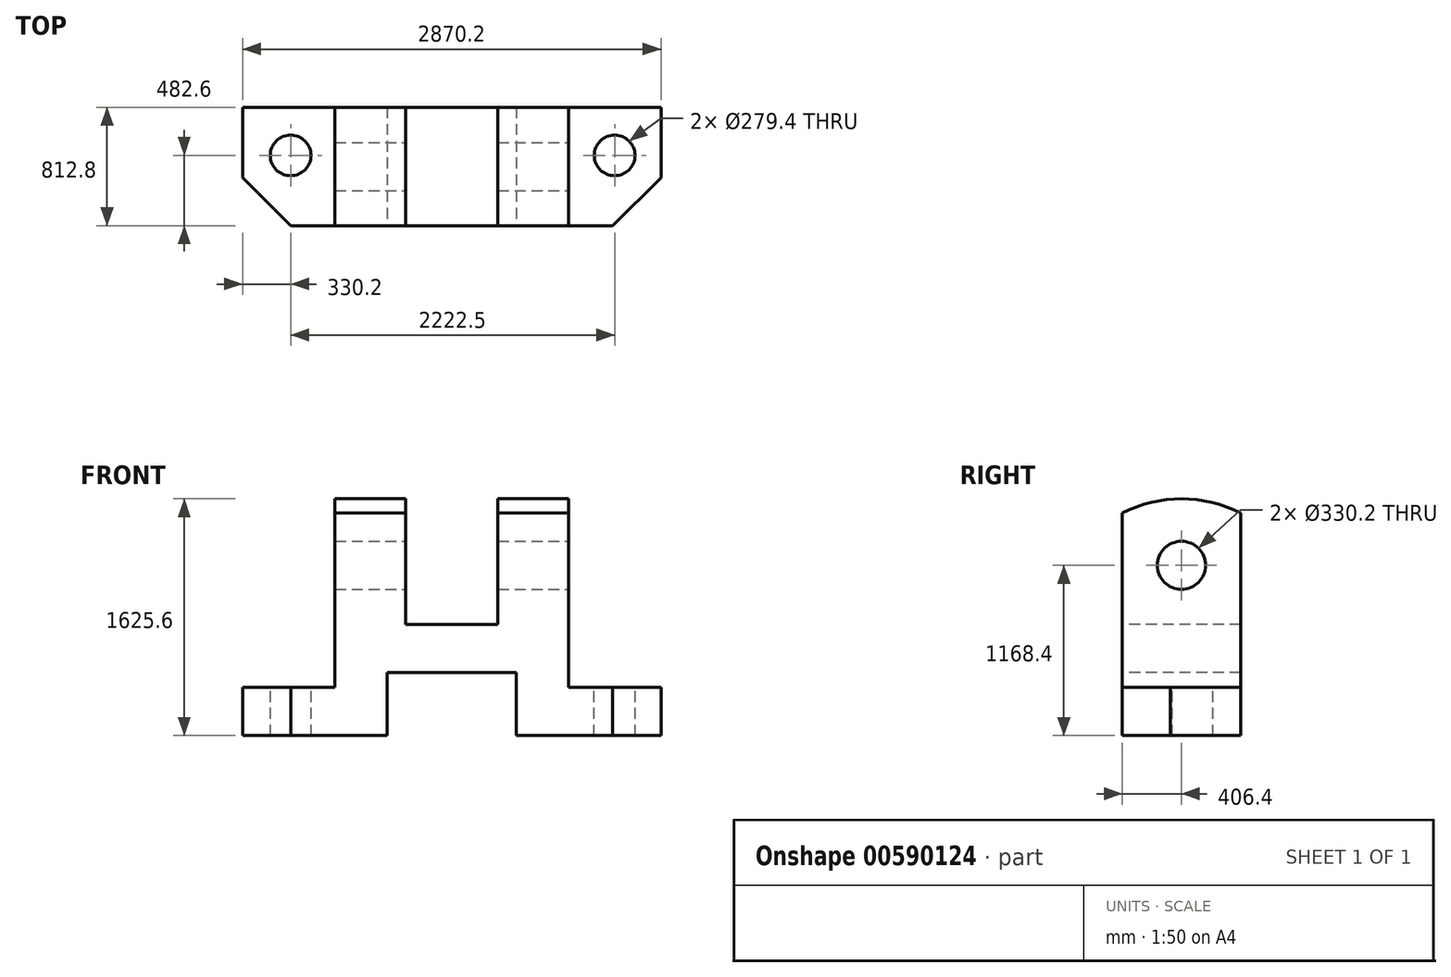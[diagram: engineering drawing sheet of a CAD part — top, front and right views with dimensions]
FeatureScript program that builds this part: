
annotation { "Feature Type Name" : "Feature", "Feature Type Description" : "" }
export const myFeature = defineFeature(function(context is Context, id is Id, definition is map)
    precondition{}
    {
        {
            var Q0;
            Q0=qCreatedBy(makeId("Front.planeOp"),FACE);
            var sketch = newSketch(context, id + "F0", { "sketchPlane" : qUnion([Q0])});
            skLineSegment(sketch, "E0.bottom", {"start": v(1435.1, 165.1) * mm, "end": v(-1435.1, 165.1) * mm});
            skLineSegment(sketch, "E0.top", {"start": v(1435.1, -165.1) * mm, "end": v(-1435.1, -165.1) * mm});
            skLineSegment(sketch, "E0.left", {"start": v(1435.1, 165.1) * mm, "end": v(1435.1, -165.1) * mm});
            skLineSegment(sketch, "E0.right", {"start": v(-1435.1, 165.1) * mm, "end": v(-1435.1, -165.1) * mm});
            skPoint(sketch, "E0.middle", {"position": v(0, 0) * mm});
            skSolve(sketch);
        }
        {
            var Q0;
            Q0=qSketchRegion(id+"F0",true);
            extrude(context, id + "F1", {"entities" : qUnion([Q0]), "depth" : 25.4 * mm});
        }
        {
            var Q0;
            Q0=qSketchRegion(id+"F0",true);
            extrude(context, id + "F2", {"entities" : qUnion([Q0]), "operationType" : NewBodyOperationType.ADD, "depth" : 812.8 * mm});
        }
        {
            var Q0;
            Q0=makeQuery(id+"F2.opExtrude","CAP_FACE",FACE,{"disambiguationData":[OSD([sQuery(id+"F0.wireOp",EDGE,"E0.bottom"),sQuery(id+"F0.wireOp",EDGE,"E0.top"),sQuery(id+"F0.wireOp",EDGE,"E0.left"),sQuery(id+"F0.wireOp",EDGE,"E0.right")])],"isStart":false});
            var sketch = newSketch(context, id + "F3", { "sketchPlane" : qUnion([Q0])});
            skLineSegment(sketch, "E1.bottom", {"start": v(-800.1, 165.1) * mm, "end": v(-317.5, 165.1) * mm});
            skLineSegment(sketch, "E1.top", {"start": v(-800.1, 1460.5) * mm, "end": v(-317.5, 1460.5) * mm});
            skLineSegment(sketch, "E1.left", {"start": v(-800.1, 165.1) * mm, "end": v(-800.1, 1460.5) * mm});
            skLineSegment(sketch, "E1.right", {"start": v(-317.5, 165.1) * mm, "end": v(-317.5, 1460.5) * mm});
            skLineSegment(sketch, "E2.bottom", {"start": v(317.5, 165.1) * mm, "end": v(800.1, 165.1) * mm});
            skLineSegment(sketch, "E2.top", {"start": v(317.5, 1460.5) * mm, "end": v(800.1, 1460.5) * mm});
            skLineSegment(sketch, "E2.left", {"start": v(317.5, 165.1) * mm, "end": v(317.5, 1460.5) * mm});
            skLineSegment(sketch, "E2.right", {"start": v(800.1, 165.1) * mm, "end": v(800.1, 1460.5) * mm});
            skSolve(sketch);
        }
        {
            var Q0;
            Q0=qSketchRegion(id+"F3",true);
            extrude(context, id + "F4", {"entities" : qUnion([Q0]), "operationType" : NewBodyOperationType.ADD, "oppositeDirection" : true, "depth" : 812.8 * mm});
        }
        {
            var Q0;
            Q0=makeQuery(id+"F4.boolean.opBoolean","MERGE",FACE,{"derivedFrom":[makeQuery(id+"F2.opExtrude","CAP_FACE",FACE,{"disambiguationData":[OSD([sQuery(id+"F0.wireOp",EDGE,"E0.bottom"),sQuery(id+"F0.wireOp",EDGE,"E0.top"),sQuery(id+"F0.wireOp",EDGE,"E0.left"),sQuery(id+"F0.wireOp",EDGE,"E0.right")])],"isStart":false}),makeQuery(id+"F4.opExtrude","CAP_FACE",FACE,{"disambiguationData":[OSD([sQuery(id+"F3.wireOp",EDGE,"E1.bottom"),sQuery(id+"F3.wireOp",EDGE,"E1.top"),sQuery(id+"F3.wireOp",EDGE,"E1.left"),sQuery(id+"F3.wireOp",EDGE,"E1.right")])],"isStart":true}),makeQuery(id+"F4.opExtrude","CAP_FACE",FACE,{"disambiguationData":[OSD([sQuery(id+"F3.wireOp",EDGE,"E2.bottom"),sQuery(id+"F3.wireOp",EDGE,"E2.top"),sQuery(id+"F3.wireOp",EDGE,"E2.left"),sQuery(id+"F3.wireOp",EDGE,"E2.right")])],"isStart":true})]});
            var sketch = newSketch(context, id + "F5", { "sketchPlane" : qUnion([Q0])});
            skLineSegment(sketch, "E3.bottom", {"start": v(-317.5, 165.1) * mm, "end": v(317.5, 165.1) * mm});
            skLineSegment(sketch, "E3.top", {"start": v(-317.5, 596.9) * mm, "end": v(317.5, 596.9) * mm});
            skLineSegment(sketch, "E3.left", {"start": v(-317.5, 165.1) * mm, "end": v(-317.5, 596.9) * mm});
            skLineSegment(sketch, "E3.right", {"start": v(317.5, 165.1) * mm, "end": v(317.5, 596.9) * mm});
            skSolve(sketch);
        }
        {
            var Q0;
            Q0=qSketchRegion(id+"F5",true);
            extrude(context, id + "F6", {"entities" : qUnion([Q0]), "operationType" : NewBodyOperationType.ADD, "oppositeDirection" : true, "depth" : 812.8 * mm});
        }
        {
            var Q0;
            Q0=makeQuery(id+"F6.boolean.opBoolean","MERGE",FACE,{"derivedFrom":[makeQuery(id+"F4.boolean.opBoolean","MERGE",FACE,{"derivedFrom":[makeQuery(id+"F2.opExtrude","CAP_FACE",FACE,{"disambiguationData":[OSD([sQuery(id+"F0.wireOp",EDGE,"E0.bottom"),sQuery(id+"F0.wireOp",EDGE,"E0.top"),sQuery(id+"F0.wireOp",EDGE,"E0.left"),sQuery(id+"F0.wireOp",EDGE,"E0.right")])],"isStart":false}),makeQuery(id+"F4.opExtrude","CAP_FACE",FACE,{"disambiguationData":[OSD([sQuery(id+"F3.wireOp",EDGE,"E1.bottom"),sQuery(id+"F3.wireOp",EDGE,"E1.top"),sQuery(id+"F3.wireOp",EDGE,"E1.left"),sQuery(id+"F3.wireOp",EDGE,"E1.right")])],"isStart":true}),makeQuery(id+"F4.opExtrude","CAP_FACE",FACE,{"disambiguationData":[OSD([sQuery(id+"F3.wireOp",EDGE,"E2.bottom"),sQuery(id+"F3.wireOp",EDGE,"E2.top"),sQuery(id+"F3.wireOp",EDGE,"E2.left"),sQuery(id+"F3.wireOp",EDGE,"E2.right")])],"isStart":true})]}),makeQuery(id+"F6.opExtrude","CAP_FACE",FACE,{"disambiguationData":[OSD([sQuery(id+"F5.wireOp",EDGE,"E3.bottom"),sQuery(id+"F5.wireOp",EDGE,"E3.top"),sQuery(id+"F5.wireOp",EDGE,"E3.left"),sQuery(id+"F5.wireOp",EDGE,"E3.right")])],"isStart":true})]});
            var sketch = newSketch(context, id + "F7", { "sketchPlane" : qUnion([Q0])});
            skLineSegment(sketch, "E4.bottom", {"start": v(-444.5, -165.1) * mm, "end": v(444.5, -165.1) * mm});
            skLineSegment(sketch, "E4.top", {"start": v(-444.5, 266.7) * mm, "end": v(444.5, 266.7) * mm});
            skLineSegment(sketch, "E4.left", {"start": v(-444.5, -165.1) * mm, "end": v(-444.5, 266.7) * mm});
            skLineSegment(sketch, "E4.right", {"start": v(444.5, -165.1) * mm, "end": v(444.5, 266.7) * mm});
            skSolve(sketch);
        }
        {
            var Q0;
            Q0=qSketchRegion(id+"F7",true);
            extrude(context, id + "F8", {"entities" : qUnion([Q0]), "operationType" : NewBodyOperationType.REMOVE, "endBound" : BoundingType.THROUGH_ALL, "oppositeDirection" : true, "depth" : 25.4 * mm});
        }
        {
            var Q0;
            {var subQ1=sQuery(id+"F0.wireOp",EDGE,"E0.left");var subQ3=sQuery(id+"F0.wireOp",EDGE,"E0.bottom");Q0=makeQuery(id+"F4.boolean.opBoolean","SPLIT",FACE,{"disambiguationData":[TD([makeQuery(id+"F1.opExtrude","SWEPT_FACE",FACE,{"disambiguationData":[OSD([subQ1])]})])],"derivedFrom":makeQuery(id+"F2.boolean.opBoolean","MERGE",FACE,{"derivedFrom":[makeQuery(id+"F1.opExtrude","SWEPT_FACE",FACE,{"disambiguationData":[OSD([subQ3])]}),makeQuery(id+"F2.opExtrude","SWEPT_FACE",FACE,{"disambiguationData":[OSD([subQ3])]})]})});}
            var sketch = newSketch(context, id + "F9", { "sketchPlane" : qUnion([Q0])});
            skCircle(sketch, "E5", {"center": v(1117.6, -330.2) * mm, "radius": 139.7 * mm});
            skPoint(sketch, "E5.centerSnap0", {"position": v(1117.6, 0) * mm});
            skCircle(sketch, "E6", {"center": v(-1104.9, -330.2) * mm, "radius": 139.7 * mm});
            skSolve(sketch);
        }
        {
            var Q0;
            Q0=qSketchRegion(id+"F9",true);
            extrude(context, id + "F10", {"entities" : qUnion([Q0]), "operationType" : NewBodyOperationType.REMOVE, "endBound" : BoundingType.THROUGH_ALL, "oppositeDirection" : true, "depth" : 25.4 * mm});
        }
        {
            var Q0;
            Q0=makeQuery(id+"F2.opExtrude","CAP_EDGE",EDGE,{"disambiguationData":[OSD([sQuery(id+"F0.wireOp",EDGE,"E0.right")])],"isStart":false});
            var Q1;
            Q1=makeQuery(id+"F2.opExtrude","CAP_EDGE",EDGE,{"disambiguationData":[OSD([sQuery(id+"F0.wireOp",EDGE,"E0.left")])],"isStart":false});
            chamfer(context, id + "F11", {"entities" : qUnion([Q0, Q1]), "chamferType" : ChamferType.OFFSET_ANGLE, "width" : 330.2 * mm, "oppositeDirection" : false, "angle" : 45 * degree, "tangentPropagation" : true});
        }
        {
            var Q0;
            Q0=makeQuery(id+"F4.opExtrude","SWEPT_FACE",FACE,{"disambiguationData":[OSD([sQuery(id+"F3.wireOp",EDGE,"E2.right")])]});
            var sketch = newSketch(context, id + "F12", { "sketchPlane" : qUnion([Q0])});
            skCircle(sketch, "E7", {"center": v(-406.4, 1003.3) * mm, "radius": 165.1 * mm});
            skPoint(sketch, "E7.centerSnap0", {"position": v(-406.4, 1460.5) * mm});
            skSolve(sketch);
        }
        {
            var Q0;
            Q0=qSketchRegion(id+"F12",true);
            extrude(context, id + "F13", {"entities" : qUnion([Q0]), "operationType" : NewBodyOperationType.ADD, "depth" : 25.4 * mm});
        }
        {
            var Q0;
            Q0=makeQuery(id+"F13.opExtrude","CAP_FACE",FACE,{"disambiguationData":[OSD([sQuery(id+"F12.wireOp",EDGE,"E7")])],"isStart":false});
            extrude(context, id + "F14", {"entities" : qUnion([Q0]), "operationType" : NewBodyOperationType.REMOVE, "endBound" : BoundingType.THROUGH_ALL, "oppositeDirection" : true, "depth" : 25.4 * mm});
        }
        {
            var Q0;
            Q0=makeQuery(id+"F12.imprint","IMPRINT",FACE,{"disambiguationData":[TD([[makeQuery(id+"F12.imprint","IMPRINT",EDGE,{"derivedFrom":sQuery(id+"F12.wireOp",EDGE,"E7")}),-1.0]])]});
            var sketch = newSketch(context, id + "F15", { "sketchPlane" : qUnion([Q0])});
            skLineSegment(sketch, "E8", {"start": v(-406.4, 1460.5) * mm, "end": v(-406.4, 571.5) * mm, "construction": true});
            skArc(sketch, "E9", {"start": v(0, 1362.17) * mm, "mid": v(-407.35, 1460.5) * mm, "end": v(-814.5, 1361.3) * mm});
            skLineSegment(sketch, "E10", {"start": v(-406.4, 1460.5) * mm, "end": v(-812.8, 1460.5) * mm});
            skLineSegment(sketch, "E11", {"start": v(-812.8, 1460.5) * mm, "end": v(-814.5, 1361.3) * mm});
            skLineSegment(sketch, "E12", {"start": v(-406.4, 1460.5) * mm, "end": v(0, 1460.5) * mm});
            skLineSegment(sketch, "E13", {"start": v(0, 1460.5) * mm, "end": v(0, 1362.17) * mm});
            skSolve(sketch);
        }
        {
            var Q0;
            Q0=qSketchRegion(id+"F15",true);
            extrude(context, id + "F16", {"entities" : qUnion([Q0]), "operationType" : NewBodyOperationType.REMOVE, "endBound" : BoundingType.THROUGH_ALL, "oppositeDirection" : true, "depth" : 25.4 * mm});
        }
    });
